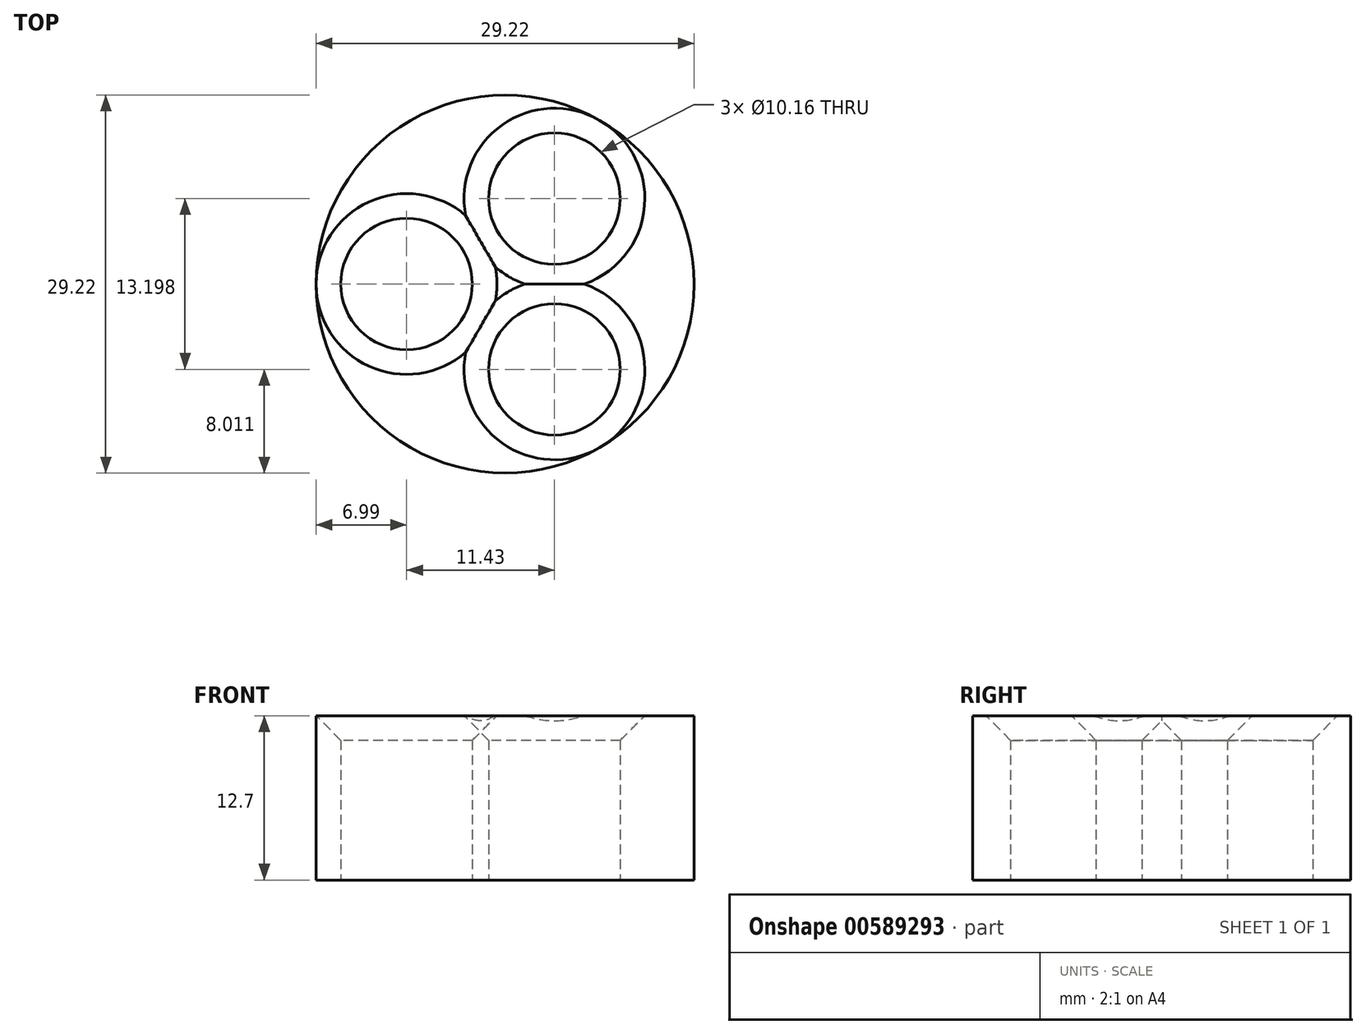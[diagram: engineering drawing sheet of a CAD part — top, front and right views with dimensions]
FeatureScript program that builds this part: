
annotation { "Feature Type Name" : "Feature", "Feature Type Description" : "" }
export const myFeature = defineFeature(function(context is Context, id is Id, definition is map)
    precondition{}
    {
        {
            var Q0;
            Q0=qCreatedBy(makeId("Top.planeOp"),FACE);
            var sketch = newSketch(context, id + "F0", { "sketchPlane" : qUnion([Q0])});
            skCircle(sketch, "E0", {"center": v(0, 0) * mm, "radius": 14.6 * mm});
            skCircle(sketch, "E1", {"center": v(3.81, 6.6) * mm, "radius": 5.08 * mm});
            skCircle(sketch, "E2.MirrorC", {"center": v(-7.62, 0) * mm, "radius": 5.08 * mm});
            skCircle(sketch, "E3.MirrorC", {"center": v(3.8, -6.6) * mm, "radius": 5.08 * mm});
            skSolve(sketch);
        }
        {
            var Q0;
            Q0 = qSketchRegion(id + "F0", true);
            extrude(context, id + "F1", {"entities" : qUnion([Q0]), "depth" : 12.7 * mm, "offsetDistance" : 25.4 * mm});
        }
        {
            var Q0;
            Q0=makeQuery(id+"F1.opExtrude","CAP_EDGE",EDGE,{"disambiguationData":[OSD([sQuery(id+"F0.wireOp",EDGE,"E2.MirrorC")])],"isStart":false});
            chamfer(context, id + "F2", {"entities" : qUnion([Q0]), "width" : 1.9 * mm, "tangentPropagation" : true});
        }
        {
            var Q0;
            Q0=makeQuery(id+"F1.opExtrude","CAP_EDGE",EDGE,{"disambiguationData":[OSD([sQuery(id+"F0.wireOp",EDGE,"E1")])],"isStart":false});
            chamfer(context, id + "F3", {"entities" : qUnion([Q0]), "width" : 1.9 * mm, "tangentPropagation" : true});
        }
        {
            var Q0;
            Q0=makeQuery(id+"F1.opExtrude","CAP_EDGE",EDGE,{"disambiguationData":[OSD([sQuery(id+"F0.wireOp",EDGE,"E3.MirrorC")])],"isStart":false});
            chamfer(context, id + "F4", {"entities" : qUnion([Q0]), "width" : 1.9 * mm, "tangentPropagation" : true});
        }
    });
